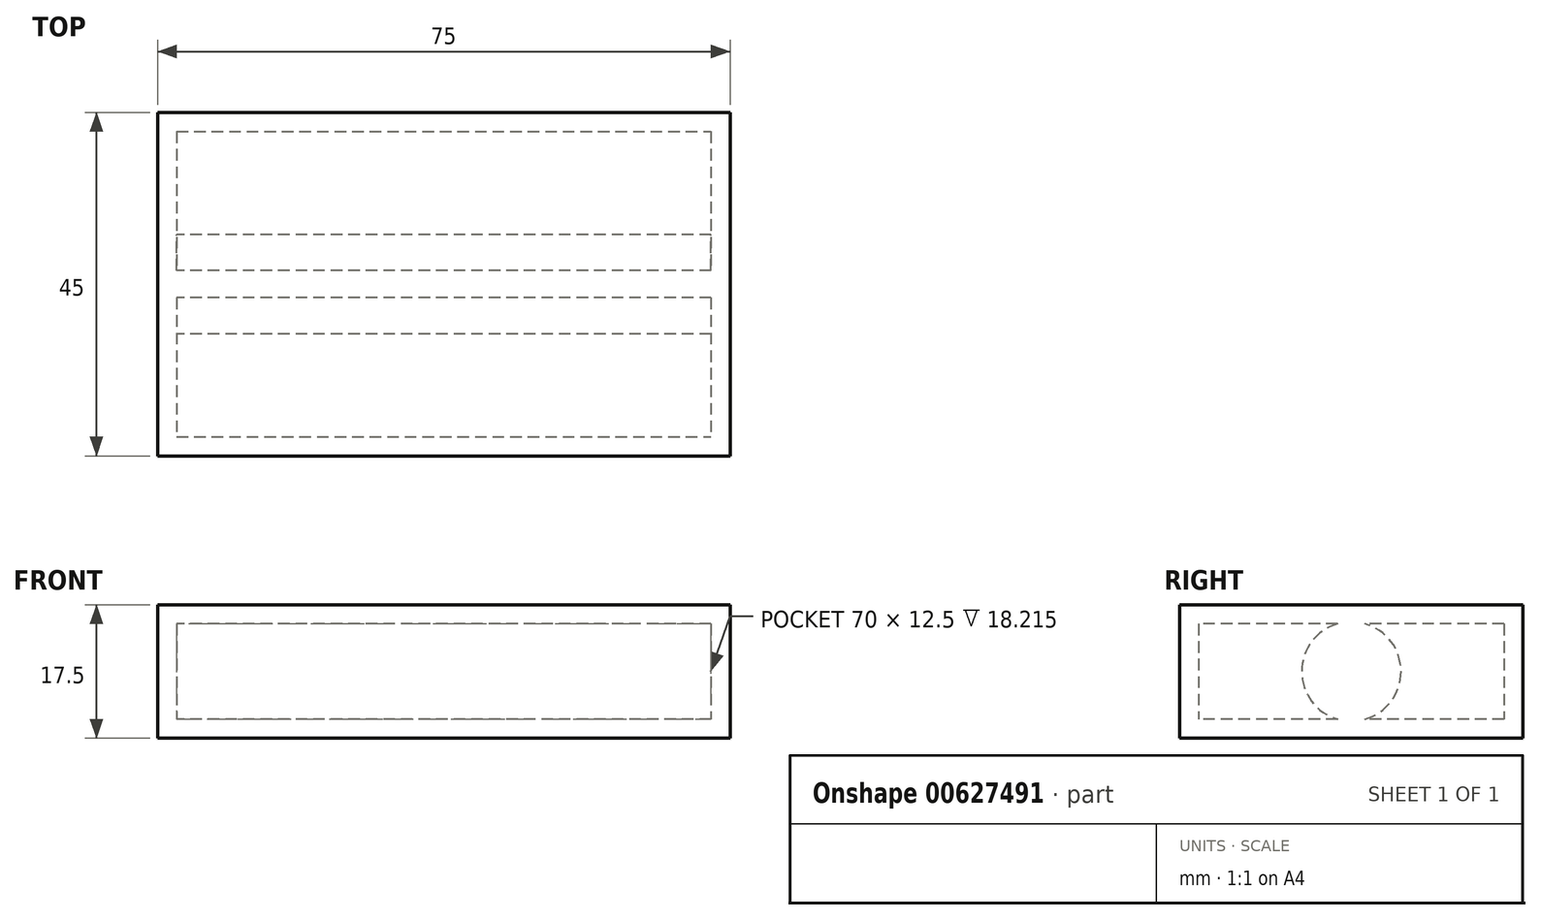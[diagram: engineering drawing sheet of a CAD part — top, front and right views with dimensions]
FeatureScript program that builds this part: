
annotation { "Feature Type Name" : "Feature", "Feature Type Description" : "" }
export const myFeature = defineFeature(function(context is Context, id is Id, definition is map)
    precondition{}
    {
        {
            var Q0;
            Q0=qCreatedBy(makeId("Top.planeOp"),FACE);
            var sketch = newSketch(context, id + "F0", { "sketchPlane" : qUnion([Q0])});
            skLineSegment(sketch, "E0.bottom", {"start": v(-37.5, 22.5) * mm, "end": v(37.5, 22.5) * mm});
            skLineSegment(sketch, "E0.top", {"start": v(-37.5, -22.5) * mm, "end": v(37.5, -22.5) * mm});
            skLineSegment(sketch, "E0.left", {"start": v(-37.5, 22.5) * mm, "end": v(-37.5, -22.5) * mm});
            skLineSegment(sketch, "E0.right", {"start": v(37.5, 22.5) * mm, "end": v(37.5, -22.5) * mm});
            skPoint(sketch, "E0.middle", {"position": v(0, 0) * mm});
            skSolve(sketch);
        }
        {
            var Q0;
            Q0 = qSketchRegion(id + "F0", true);
            extrude(context, id + "F1", {"entities" : qUnion([Q0]), "endBound" : BoundingType.SYMMETRIC, "depth" : 15 * mm, "offsetDistance" : 25 * mm});
        }
        {
            var Q0;
            Q0=makeQuery(id+"F1.opExtrude","CAP_FACE",FACE,{"disambiguationData":[OSD([sQuery(id+"F0.wireOp",EDGE,"E0.bottom"),sQuery(id+"F0.wireOp",EDGE,"E0.top"),sQuery(id+"F0.wireOp",EDGE,"E0.left"),sQuery(id+"F0.wireOp",EDGE,"E0.right")])],"isStart":false});
            shell(context, id + "F2", {"entities" : qUnion([Q0]), "thickness" : 2.5 * mm});
        }
        {
            var Q0;
            Q0=makeQuery(id+"F1.opExtrude","CAP_FACE",FACE,{"disambiguationData":[OSD([sQuery(id+"F0.wireOp",EDGE,"E0.bottom"),sQuery(id+"F0.wireOp",EDGE,"E0.top"),sQuery(id+"F0.wireOp",EDGE,"E0.left"),sQuery(id+"F0.wireOp",EDGE,"E0.right")])],"isStart":false});
            var sketch = newSketch(context, id + "F3", { "sketchPlane" : qUnion([Q0])});
            skLineSegment(sketch, "E1.0.0", {"start": v(-37.5, 22.5) * mm, "end": v(-37.5, -22.5) * mm});
            skLineSegment(sketch, "E1.0.1", {"start": v(-37.5, -22.5) * mm, "end": v(37.5, -22.5) * mm});
            skLineSegment(sketch, "E1.0.2", {"start": v(37.5, -22.5) * mm, "end": v(37.5, 22.5) * mm});
            skLineSegment(sketch, "E1.0.3", {"start": v(37.5, 22.5) * mm, "end": v(-37.5, 22.5) * mm});
            skSolve(sketch);
        }
        {
            var Q0;
            Q0 = qSketchRegion(id + "F3", true);
            extrude(context, id + "F4", {"entities" : qUnion([Q0]), "operationType" : NewBodyOperationType.ADD, "depth" : 2.5 * mm, "offsetDistance" : 25 * mm});
        }
        {
            var Q0;
            Q0=qCreatedBy(makeId("Right.planeOp"),FACE);
            var sketch = newSketch(context, id + "F5", { "sketchPlane" : qUnion([Q0])});
            skCircle(sketch, "E2", {"center": v(0, 1.25) * mm, "radius": 6.5 * mm});
            skSolve(sketch);
        }
        {
            var Q0;
            Q0 = qSketchRegion(id + "F5", true);
            extrude(context, id + "F6", {"entities" : qUnion([Q0]), "operationType" : NewBodyOperationType.ADD, "endBound" : BoundingType.SYMMETRIC, "depth" : 74 * mm, "offsetDistance" : 25 * mm});
        }
    });
